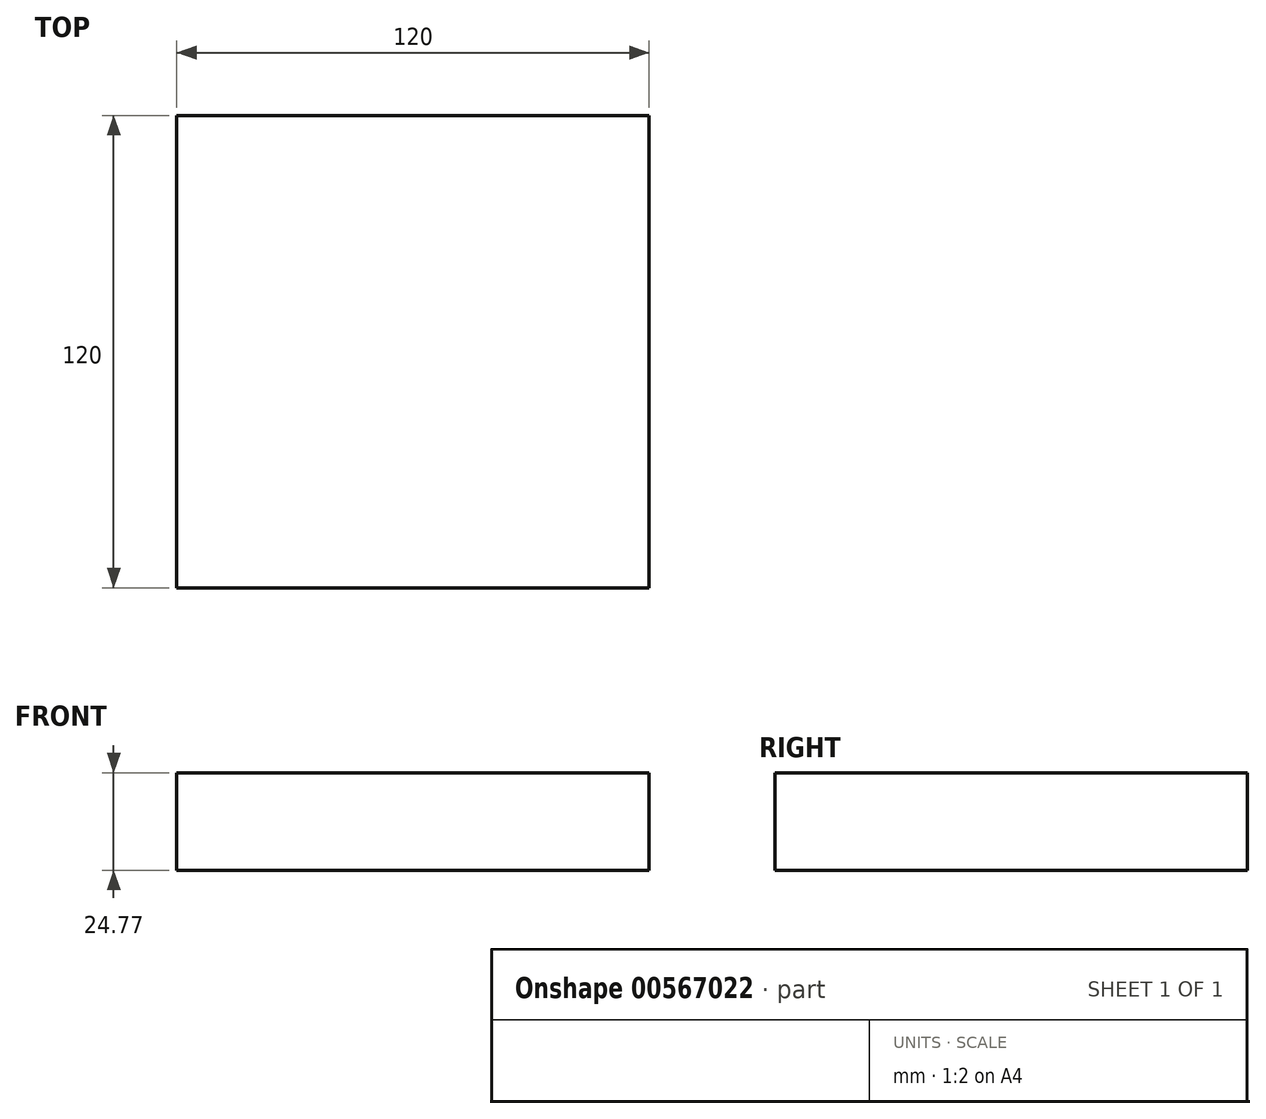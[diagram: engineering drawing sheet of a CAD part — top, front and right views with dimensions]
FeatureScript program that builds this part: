
annotation { "Feature Type Name" : "Feature", "Feature Type Description" : "" }
export const myFeature = defineFeature(function(context is Context, id is Id, definition is map)
    precondition{}
    {
        {
            var Q0;
            Q0=qCreatedBy(makeId("Top.planeOp"),FACE);
            var sketch = newSketch(context, id + "F0", { "sketchPlane" : qUnion([Q0])});
            skLineSegment(sketch, "E0.bottom", {"start": v(60, 60) * mm, "end": v(-60, 60) * mm});
            skLineSegment(sketch, "E0.top", {"start": v(60, -60) * mm, "end": v(-60, -60) * mm});
            skLineSegment(sketch, "E0.left", {"start": v(60, 60) * mm, "end": v(60, -60) * mm});
            skLineSegment(sketch, "E0.right", {"start": v(-60, 60) * mm, "end": v(-60, -60) * mm});
            skPoint(sketch, "E0.middle", {"position": v(0, 0) * mm});
            skSolve(sketch);
        }
        {
            var Q0;
            Q0 = qSketchRegion(id + "F0", true);
            extrude(context, id + "F1", {"entities" : qUnion([Q0]), "depth" : 24.76 * mm, "offsetDistance" : 25 * mm});
        }
    });
